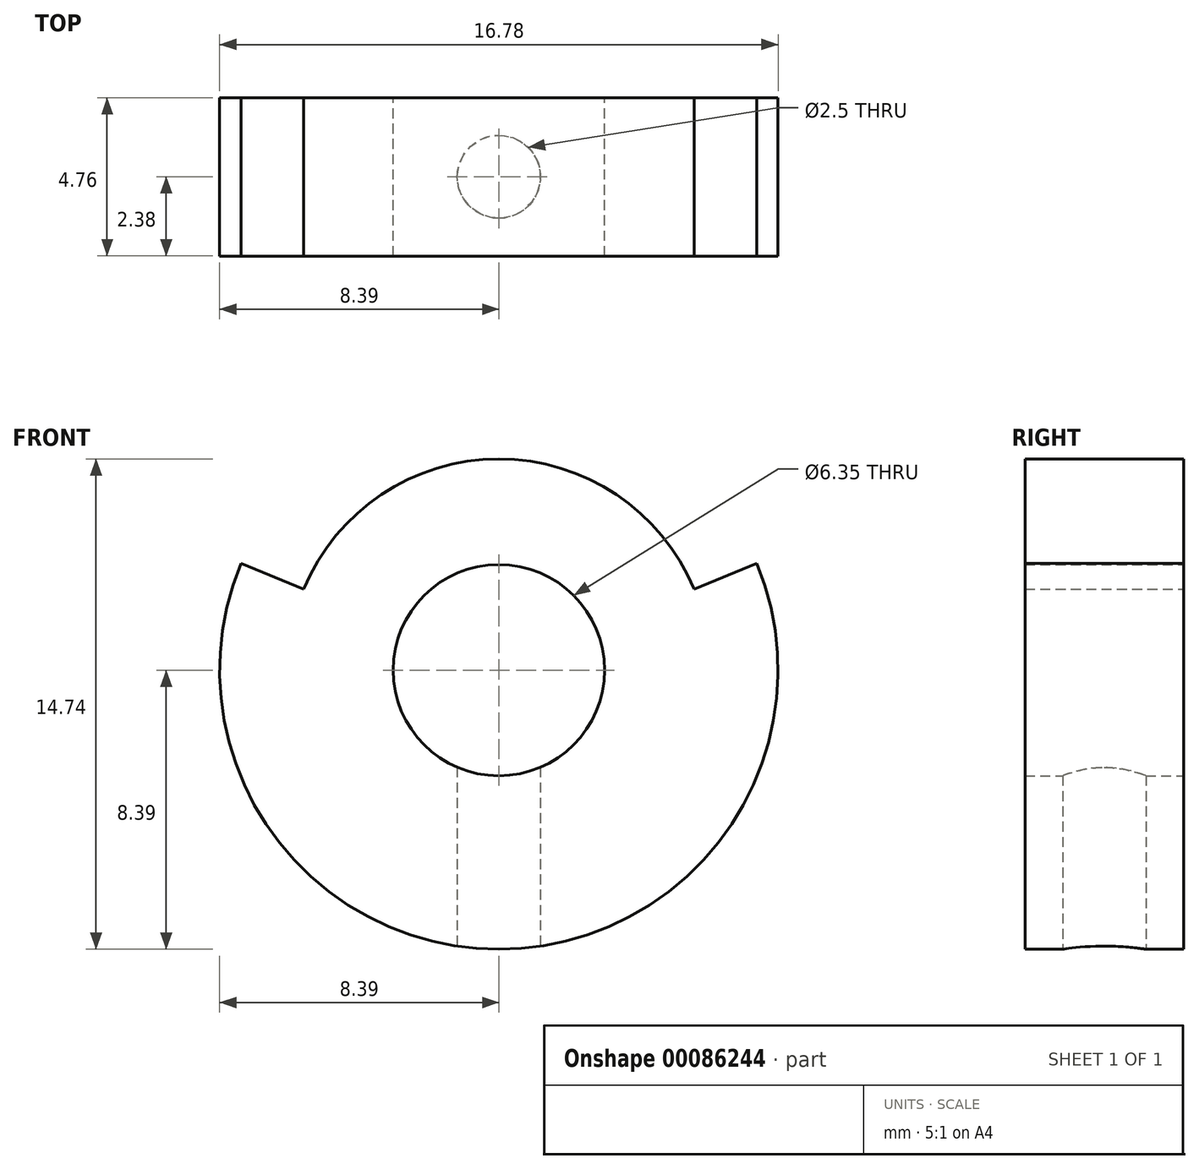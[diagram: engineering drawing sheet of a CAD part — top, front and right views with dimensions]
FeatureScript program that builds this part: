
annotation { "Feature Type Name" : "Feature", "Feature Type Description" : "" }
export const myFeature = defineFeature(function(context is Context, id is Id, definition is map)
    precondition{}
    {
        {
            var Q0;
            Q0=qCreatedBy(makeId("Front.planeOp"),FACE);
            var sketch = newSketch(context, id + "F0", { "sketchPlane" : qUnion([Q0])});
            skArc(sketch, "E0", {"start": v(-7.75, 3.2) * mm, "mid": v(0, -8.39) * mm, "end": v(7.75, 3.2) * mm});
            skArc(sketch, "E1", {"start": v(5.87, 2.43) * mm, "mid": v(0, 6.35) * mm, "end": v(-5.87, 2.43) * mm});
            skLineSegment(sketch, "E2", {"start": v(-5.87, 2.43) * mm, "end": v(-7.75, 3.2) * mm});
            skLineSegment(sketch, "E3", {"start": v(5.87, 2.43) * mm, "end": v(7.75, 3.2) * mm});
            skLineSegment(sketch, "E4", {"start": v(-7.75, 3.2) * mm, "end": v(7.75, 3.2) * mm, "construction": true});
            skCircle(sketch, "E5", {"center": v(0, 0) * mm, "radius": 3.17 * mm});
            skSolve(sketch);
        }
        {
            var Q0;
            Q0=makeQuery(id+"F0.imprint","IMPRINT",FACE,{"disambiguationData":[TD([[makeQuery(id+"F0.imprint","IMPRINT",EDGE,{"derivedFrom":sQuery(id+"F0.wireOp",EDGE,"E0")}),1.0]])]});
            extrude(context, id + "F1", {"entities" : qUnion([Q0]), "depth" : ((3 / 16) * 25.4) * mm, "symmetric" : true});
        }
        {
            var Q0;
            Q0=qCreatedBy(makeId("Top.planeOp"),FACE);
            var sketch = newSketch(context, id + "F2", { "sketchPlane" : qUnion([Q0])});
            skPoint(sketch, "E6", {"position": v(0, 0) * mm});
            skSolve(sketch);
        }
        {
            var Q0;
            Q0=sQuery(id+"F2.wireOp",VERTEX,"E6");
            var Q1;
            Q1=makeQuery(id+"F1.opExtrude","SWEPT_BODY",BODY,{"disambiguationData":[OSD([sQuery(id+"F0.wireOp",EDGE,"E0"),sQuery(id+"F0.wireOp",EDGE,"E1"),sQuery(id+"F0.wireOp",EDGE,"E2"),sQuery(id+"F0.wireOp",EDGE,"E3"),sQuery(id+"F0.wireOp",EDGE,"E5")])]});
            hole(context, id + "F3", {"style" : HoleStyle.SIMPLE, "endStyle" : HoleEndStyle.THROUGH, "standardTappedOrClearance" : lookupTablePath({ "standard" : "ISO", "engagement" : "75%", "pitch" : "0.5 mm", "size" : "M3", "type" : "Tapped" }), "standardBlindInLast" : lookupTablePath({ "standard" : "ISO", "engagement" : "75%", "pitch" : "0.5 mm", "size" : "M3", "type" : "Tapped" }), "holeDiameter" : 2.5 * mm, "locations" : qUnion([Q0]), "scope" : qUnion([Q1]), "isTappedThrough" : true, "majorDiameter" : 3 * mm, "showTappedDepth" : true});
        }
    });
